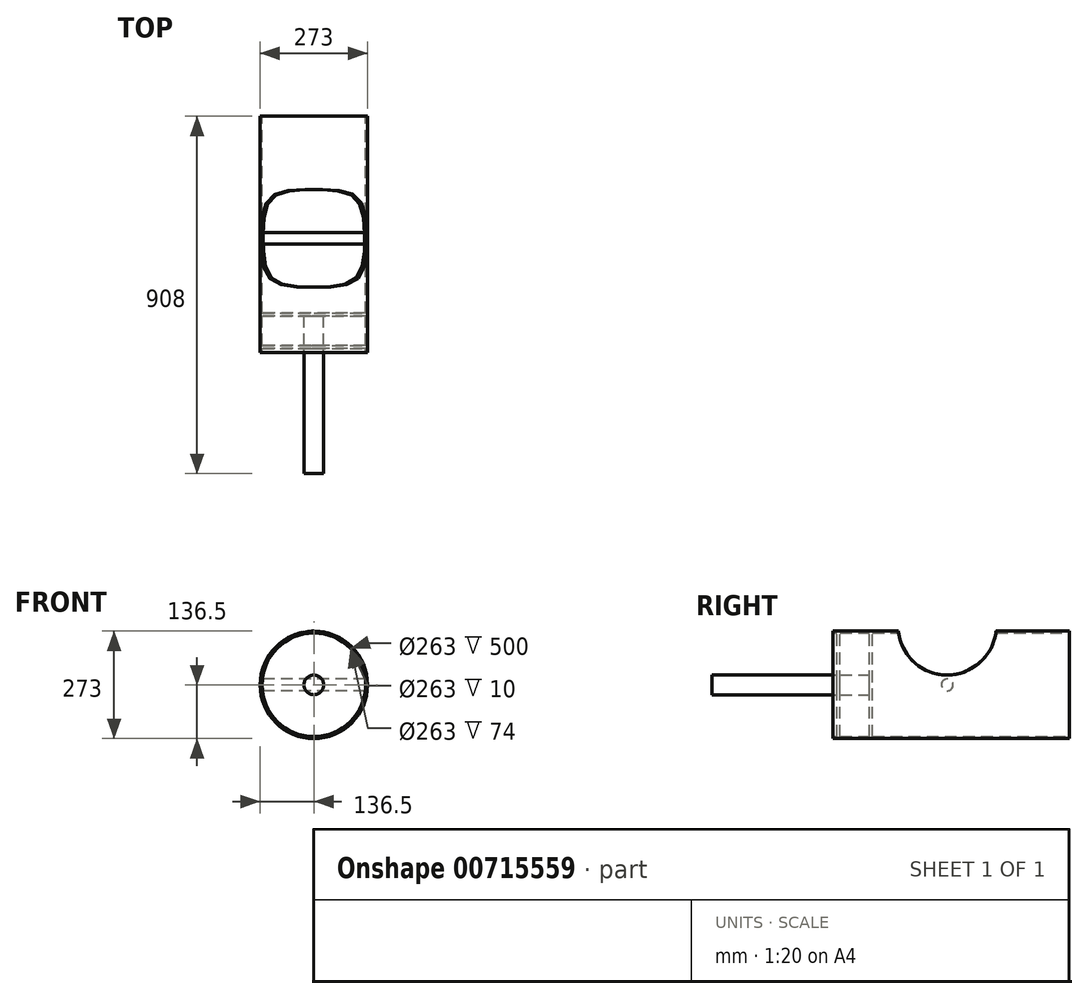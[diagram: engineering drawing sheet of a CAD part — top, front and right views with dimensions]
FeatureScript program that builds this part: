
annotation { "Feature Type Name" : "Feature", "Feature Type Description" : "" }
export const myFeature = defineFeature(function(context is Context, id is Id, definition is map)
    precondition{}
    {
        {
            var Q0;
            Q0=qCreatedBy(makeId("Front.planeOp"),FACE);
            var sketch = newSketch(context, id + "F0", { "sketchPlane" : qUnion([Q0])});
            skCircle(sketch, "E0", {"center": v(0, 0) * mm, "radius": 136.5 * mm});
            skCircle(sketch, "E1", {"center": v(0, 0) * mm, "radius": 131.5 * mm});
            skSolve(sketch);
        }
        {
            var Q0;
            Q0 = qSketchRegion(id + "F0", true);
            extrude(context, id + "F1", {"entities" : qUnion([Q0]), "depth" : 600 * mm, "offsetDistance" : 25 * mm});
        }
        {
            var Q0;
            Q0=makeQuery(id+"F1.opExtrude","CAP_FACE",FACE,{"disambiguationData":[OSD([sQuery(id+"F0.wireOp",EDGE,"E0"),sQuery(id+"F0.wireOp",EDGE,"E1")])],"isStart":false});
            cPlane(context, id + "F2", {"entities" : qUnion([Q0]), "cplaneType" : CPlaneType.OFFSET, "offset" : 100 * mm, "oppositeDirection" : true, "width" : 150 * mm, "height" : 150 * mm});
        }
        {
            var Q0;
            Q0=qCreatedBy(id+"F2.planeOp",FACE);
            var sketch = newSketch(context, id + "F3", { "sketchPlane" : qUnion([Q0])});
            skCircle(sketch, "E2", {"center": v(0, 0) * mm, "radius": 131.5 * mm});
            skSolve(sketch);
        }
        {
            var Q0;
            Q0 = qSketchRegion(id + "F3", true);
            extrude(context, id + "F4", {"entities" : qUnion([Q0]), "operationType" : NewBodyOperationType.ADD, "depth" : 8 * mm, "offsetDistance" : 25 * mm});
        }
        {
            var Q0;
            Q0=makeQuery(id+"F4.opExtrude","CAP_FACE",FACE,{"disambiguationData":[OSD([sQuery(id+"F3.wireOp",EDGE,"E2")])],"isStart":false});
            var sketch = newSketch(context, id + "F5", { "sketchPlane" : qUnion([Q0])});
            skCircle(sketch, "E3", {"center": v(0, 0) * mm, "radius": 25 * mm});
            skSolve(sketch);
        }
        {
            var Q0;
            Q0 = qSketchRegion(id + "F5", true);
            extrude(context, id + "F6", {"entities" : qUnion([Q0]), "operationType" : NewBodyOperationType.ADD, "depth" : 400 * mm, "offsetDistance" : 25 * mm});
        }
        {
            var Q0;
            Q0=qCreatedBy(makeId("Right.planeOp"),FACE);
            var sketch = newSketch(context, id + "F7", { "sketchPlane" : qUnion([Q0])});
            skCircle(sketch, "E4", {"center": v(-310, 0) * mm, "radius": 15 * mm});
            skSolve(sketch);
        }
        {
            var Q0;
            Q0 = qSketchRegion(id + "F7", true);
            extrude(context, id + "F8", {"entities" : qUnion([Q0]), "operationType" : NewBodyOperationType.ADD, "depth" : 154 * mm, "offsetDistance" : 25 * mm});
        }
        {
            var Q0;
            Q0 = qSketchRegion(id + "F7", true);
            extrude(context, id + "F9", {"entities" : qUnion([Q0]), "operationType" : NewBodyOperationType.ADD, "oppositeDirection" : true, "depth" : 149 * mm, "offsetDistance" : 25 * mm});
        }
        {
            var Q0;
            Q0=makeQuery(id+"F8.opExtrude","CAP_FACE",FACE,{"disambiguationData":[OSD([sQuery(id+"F7.wireOp",EDGE,"E4")])],"isStart":false});
            var sketch = newSketch(context, id + "F10", { "sketchPlane" : qUnion([Q0])});
            skCircle(sketch, "E5", {"center": v(-310, 150) * mm, "radius": 125 * mm});
            skSolve(sketch);
        }
        {
            var Q0;
            Q0 = qSketchRegion(id + "F10", true);
            extrude(context, id + "F11", {"entities" : qUnion([Q0]), "operationType" : NewBodyOperationType.REMOVE, "oppositeDirection" : true, "depth" : 348 * mm, "offsetDistance" : 25 * mm});
        }
        {
            var Q0;
            Q0=makeQuery(id+"F6.opExtrude","CAP_FACE",FACE,{"disambiguationData":[OSD([sQuery(id+"F5.wireOp",EDGE,"E3")])],"isStart":false});
            var sketch = newSketch(context, id + "F12", { "sketchPlane" : qUnion([Q0])});
            skCircle(sketch, "E6", {"center": v(0, 0) * mm, "radius": 175 * mm});
            skCircle(sketch, "E7", {"center": v(0, 0) * mm, "radius": 136.5 * mm});
            skSolve(sketch);
        }
        {
            var Q0;
            Q0 = qSketchRegion(id + "F12", true);
            extrude(context, id + "F13", {"entities" : qUnion([Q0]), "operationType" : NewBodyOperationType.REMOVE, "oppositeDirection" : true, "depth" : 1133 * mm, "offsetDistance" : 25 * mm});
        }
        {
            var Q0;
            Q0=makeQuery(id+"F1.opExtrude","CAP_FACE",FACE,{"disambiguationData":[OSD([sQuery(id+"F0.wireOp",EDGE,"E0"),sQuery(id+"F0.wireOp",EDGE,"E1")])],"isStart":false});
            cPlane(context, id + "F14", {"entities" : qUnion([Q0]), "cplaneType" : CPlaneType.OFFSET, "offset" : 10 * mm, "oppositeDirection" : true, "width" : 150 * mm, "height" : 150 * mm});
        }
        {
            var Q0;
            Q0=qCreatedBy(id+"F14.planeOp",FACE);
            var sketch = newSketch(context, id + "F15", { "sketchPlane" : qUnion([Q0])});
            skCircle(sketch, "E8", {"center": v(0, 0) * mm, "radius": 25 * mm});
            skCircle(sketch, "E9", {"center": v(0, 0) * mm, "radius": 136.5 * mm});
            skSolve(sketch);
        }
        {
            var Q0;
            Q0 = qSketchRegion(id + "F15", true);
            extrude(context, id + "F16", {"entities" : qUnion([Q0]), "operationType" : NewBodyOperationType.ADD, "oppositeDirection" : true, "depth" : 8 * mm, "offsetDistance" : 25 * mm});
        }
    });
